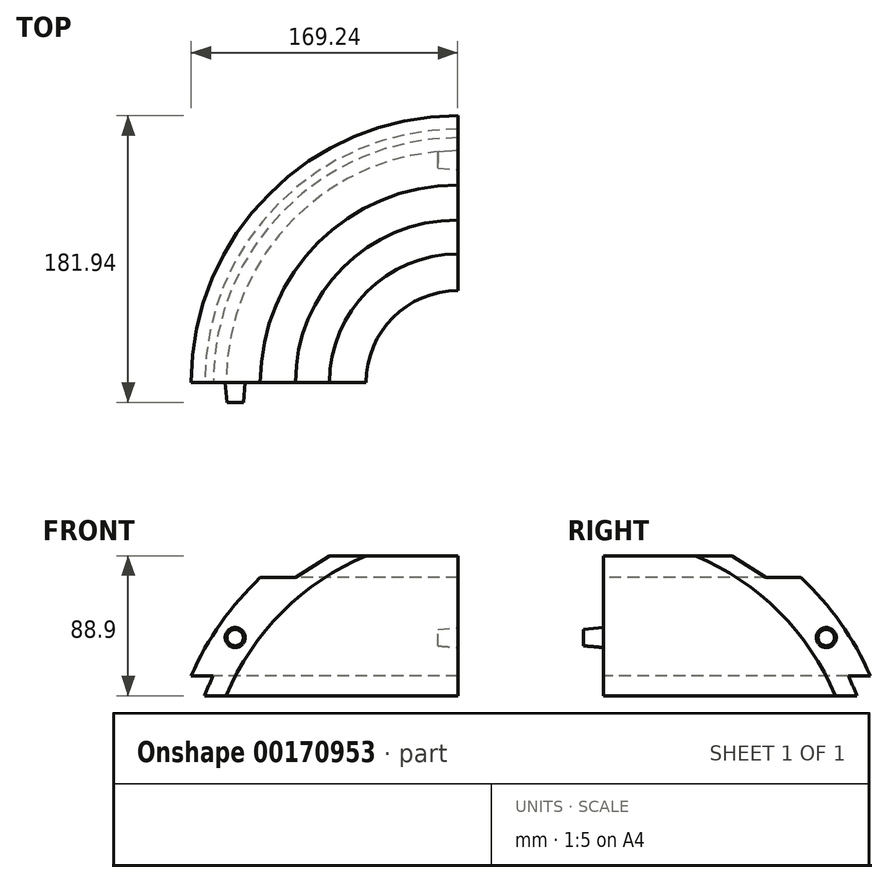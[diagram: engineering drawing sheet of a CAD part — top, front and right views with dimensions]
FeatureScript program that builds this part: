
annotation { "Feature Type Name" : "Feature", "Feature Type Description" : "" }
export const myFeature = defineFeature(function(context is Context, id is Id, definition is map)
    precondition{}
    {
        {
            var Q0;
            Q0=qCreatedBy(makeId("Front.planeOp"),FACE);
            var sketch = newSketch(context, id + "F0", { "sketchPlane" : qUnion([Q0])});
            skArc(sketch, "E0", {"start": v(-130.77, 138.53) * mm, "mid": v(-155.83, 109.58) * mm, "end": v(-174.6, 76.2) * mm});
            skArc(sketch, "E1", {"start": v(-160.64, 76.2) * mm, "mid": v(-163.48, 69.9) * mm, "end": v(-166.07, 63.5) * mm});
            skLineSegment(sketch, "E2", {"start": v(-5.36, 76.2) * mm, "end": v(-146.46, 76.2) * mm});
            skLineSegment(sketch, "E3", {"start": v(-5.36, 152.4) * mm, "end": v(-63.5, 152.4) * mm});
            skArc(sketch, "E4", {"start": v(-63.5, 152.4) * mm, "mid": v(-116.74, 116.74) * mm, "end": v(-152.4, 63.5) * mm});
            skLineSegment(sketch, "E5", {"start": v(-166.07, 63.5) * mm, "end": v(-152.4, 63.5) * mm});
            skLineSegment(sketch, "E6", {"start": v(-174.6, 76.2) * mm, "end": v(-160.64, 76.2) * mm});
            skLineSegment(sketch, "E7", {"start": v(-130.77, 138.53) * mm, "end": v(-108.44, 138.53) * mm});
            skLineSegment(sketch, "E8", {"start": v(-5.36, 152.4) * mm, "end": v(-5.36, 76.2) * mm});
            skLineSegment(sketch, "E9", {"start": v(-63.5, 152.4) * mm, "end": v(-63.5, 152.4) * mm});
            skLineSegment(sketch, "E10", {"start": v(-86.8, 152.4) * mm, "end": v(-108.44, 138.53) * mm});
            skLineSegment(sketch, "E11", {"start": v(-63.5, 152.4) * mm, "end": v(-86.8, 152.4) * mm});
            skSolve(sketch);
        }
        {
            var Q0;
            Q0=makeQuery(id+"F0.imprint","IMPRINT",FACE,{"disambiguationData":[TD([[makeQuery(id+"F0.imprint","IMPRINT",EDGE,{"derivedFrom":sQuery(id+"F0.wireOp",EDGE,"E0")}),1.0]])]});
            var Q1;
            Q1=sQuery(id+"F0.wireOp",EDGE,"E8");
            revolve(context, id + "F1", {"entities" : qUnion([Q0]), "axis" : qUnion([Q1]), "revolveType" : RevolveType.ONE_DIRECTION, "angle" : 90 * degree});
        }
        {
            var Q0;
            Q0=makeQuery(id+"F1.opRevolve","CAP_FACE",FACE,{"disambiguationData":[OSD([sQuery(id+"F0.wireOp",EDGE,"E0"),sQuery(id+"F0.wireOp",EDGE,"E1"),sQuery(id+"F0.wireOp",EDGE,"E3"),sQuery(id+"F0.wireOp",EDGE,"E4"),sQuery(id+"F0.wireOp",EDGE,"E5"),sQuery(id+"F0.wireOp",EDGE,"E6"),sQuery(id+"F0.wireOp",EDGE,"E7"),sQuery(id+"F0.wireOp",EDGE,"E9"),sQuery(id+"F0.wireOp",EDGE,"E10"),sQuery(id+"F0.wireOp",EDGE,"Pi2banda-vJtO-WxuW-bEJG-y83UNW9jW79c")])],"isStart":true});
            var sketch = newSketch(context, id + "F2", { "sketchPlane" : qUnion([Q0])});
            skCircle(sketch, "E12", {"center": v(-146.72, 100.43) * mm, "radius": 6.35 * mm});
            skSolve(sketch);
        }
        {
            var Q0;
            Q0 = qSketchRegion(id + "F2", true);
            extrude(context, id + "F3", {"entities" : qUnion([Q0]), "operationType" : NewBodyOperationType.ADD, "depth" : 12.7 * mm, "hasDraft" : true, "draftAngle" : 5 * degree, "draftPullDirection" : true});
        }
        {
            var Q0;
            Q0=makeQuery(id+"F1.opRevolve","CAP_FACE",FACE,{"disambiguationData":[OSD([sQuery(id+"F0.wireOp",EDGE,"E0"),sQuery(id+"F0.wireOp",EDGE,"E1"),sQuery(id+"F0.wireOp",EDGE,"E3"),sQuery(id+"F0.wireOp",EDGE,"E4"),sQuery(id+"F0.wireOp",EDGE,"E5"),sQuery(id+"F0.wireOp",EDGE,"E6"),sQuery(id+"F0.wireOp",EDGE,"E7"),sQuery(id+"F0.wireOp",EDGE,"E9"),sQuery(id+"F0.wireOp",EDGE,"E10"),sQuery(id+"F0.wireOp",EDGE,"Pi2banda-vJtO-WxuW-bEJG-y83UNW9jW79c")])],"isStart":false});
            var sketch = newSketch(context, id + "F4", { "sketchPlane" : qUnion([Q0])});
            skCircle(sketch, "E13", {"center": v(141.37, 100.43) * mm, "radius": 6.35 * mm});
            skSolve(sketch);
        }
        {
            var Q0;
            Q0=makeQuery(id+"F4.imprint","IMPRINT",FACE,{"disambiguationData":[TD([[makeQuery(id+"F4.imprint","IMPRINT",EDGE,{"derivedFrom":sQuery(id+"F4.wireOp",EDGE,"E13")}),1.0]])]});
            var Q1;
            Q1=sQuery(id+"F4.wireOp",EDGE,"E13");
            extrude(context, id + "F5", {"entities" : qUnion([Q0]), "operationType" : NewBodyOperationType.REMOVE, "surfaceEntities" : qUnion([Q1]), "oppositeDirection" : true, "depth" : 12.7 * mm, "hasDraft" : true, "draftAngle" : 5 * degree, "draftPullDirection" : true});
        }
    });
